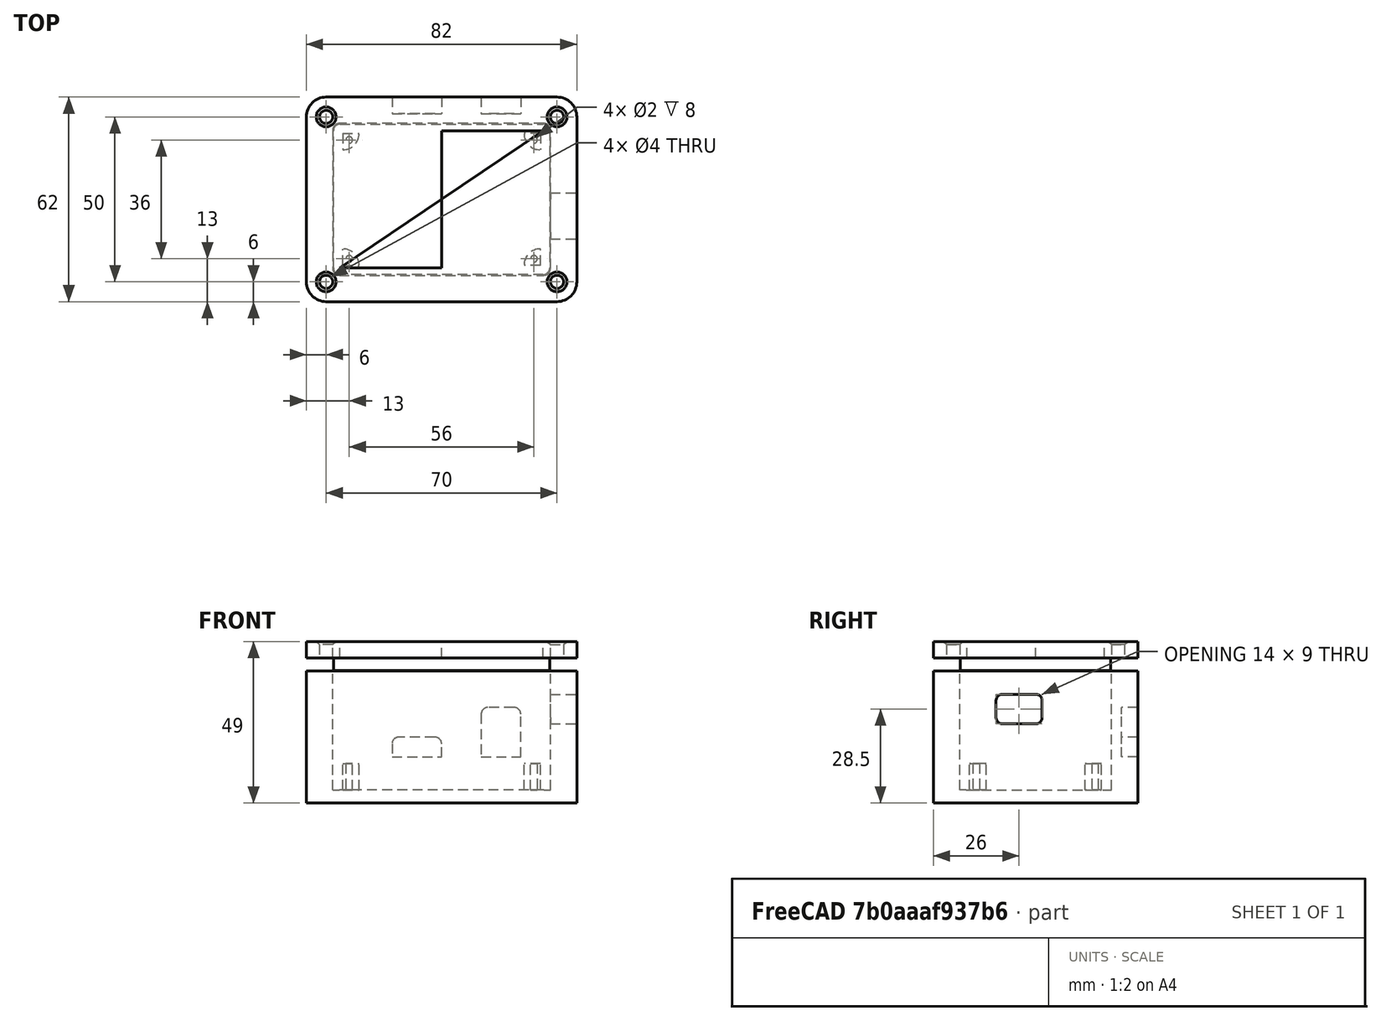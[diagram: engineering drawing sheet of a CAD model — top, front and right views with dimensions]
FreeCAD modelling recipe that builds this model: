
FCSTD DOCUMENT  (FreeCAD 0.20R29177 (Git))
Label: weatherstation
License: All rights reserved
LicenseURL: http://en.wikipedia.org/wiki/All_rights_reserved
objects: Sketcher::SketchObject×9, PartDesign::Pocket×5, PartDesign::Pad×4, PartDesign::Mirrored×4, PartDesign::MultiTransform×2, PartDesign::Body×2, Spreadsheet::Sheet×1, PartDesign::Chamfer×1
note: 37 computed .brp shape members not serialized (recipe doc carries the construction recipe); baked Part::Feature solids carry a one-line shape summary decoded from their .brp

FEATURE [Sketcher::SketchObject] Sketch  label="box"
  AttachmentOffset = pos=(0,0,-4) rot=(0,0,1;0rad)
  FullyConstrained = true
  MapMode = 5
  Placement = pos=(0,0,-4) rot=(0,0,1;0rad)
  Support = -> [XY_Plane]
  expr: .AttachmentOffset.Base.z = -Spreadsheet.box_wall_thickness
  expr: Constraints[16] = Spreadsheet.box_length
  expr: Constraints[17] = Spreadsheet.box_width
  expr: Constraints[18] = Spreadsheet.outside_radius
  sketch-geometry (8):
    g0: LineSegment StartX=-35 StartY=31 StartZ=0 EndX=35 EndY=31 EndZ=0
    g1: LineSegment StartX=41 StartY=25 StartZ=0 EndX=41 EndY=-25 EndZ=0
    g2: LineSegment StartX=35 StartY=-31 StartZ=0 EndX=-35 EndY=-31 EndZ=0
    g3: LineSegment StartX=-41 StartY=-25 StartZ=0 EndX=-41 EndY=25 EndZ=0
    g4: ArcOfCircle CenterX=-35 CenterY=25 CenterZ=0 NormalX=0 NormalY=0 NormalZ=1 AngleXU=0 Radius=6 StartAngle=1.5708 EndAngle=3.14159
    g5: ArcOfCircle CenterX=35 CenterY=25 CenterZ=0 NormalX=0 NormalY=0 NormalZ=1 AngleXU=0 Radius=6 StartAngle=-1.994e-12 EndAngle=1.5708
    g6: ArcOfCircle CenterX=35 CenterY=-25 CenterZ=0 NormalX=0 NormalY=0 NormalZ=1 AngleXU=0 Radius=6 StartAngle=4.71239 EndAngle=6.28319
    g7: ArcOfCircle CenterX=-35 CenterY=-25 CenterZ=0 NormalX=0 NormalY=0 NormalZ=1 AngleXU=0 Radius=6 StartAngle=3.14159 EndAngle=4.71239
  constraints (19):
    c: Horizontal(g0)
    c: Horizontal(g2)
    c: Vertical(g1)
    c: Vertical(g3)
    c: Tangent(g0,g4) = 1.5708
    c: Tangent(g3,g4) = 1.5708
    c: Tangent(g0,g5) = 1.5708
    c: Tangent(g1,g5) = 1.5708
    c: Tangent(g1,g6) = 1.5708
    c: Tangent(g2,g6) = 1.5708
    c: Tangent(g2,g7) = 1.5708
    c: Tangent(g3,g7) = 1.5708
    c: Equal(g4,g5)
    c: Equal(g5,g6)
    c: Equal(g6,g7)
    c: Symmetric(g4,g6,g-1)
    c: DistanceX(g0,g0) = 70
    c: DistanceY(g1,g1) = 50
    c: Radius(g4) = 6
FEATURE [PartDesign::Pad] Pad
  Direction = (0,0,1)
  Length = 40
  Length2 = 10
  Profile = -> Sketch
  ReferenceAxis = -> Sketch [N_Axis]
  Type = 0
  expr: Length = Spreadsheet.box_height
FEATURE [Spreadsheet::Sheet] Spreadsheet
  cells = A2=box_length; B2(box_length)=70; A3=box_width; B3(box_width)=50; A4=box_height; B4(box_height)=40; A5=outside_radius; B5(outside_radius)==B7 + 2; C5=Calculated; A6=inside_radius; B6(inside_radius)==B7 - 2; C6=Calculated; A7=box_wall_thickness; B7(box_wall_thickness)=4; A8=hole_diameter; B8(hole_diameter)=2; A9=lug_height; B9(lug_height)==B7 * 2; C9=Calculated; A10=lug_radius; B10(lug_radius)==B8 * 2.5; C10=Calculated; A11=hole_center_length; B11(hole_center_length)==B13 / 2 - B8; C11=Calculated; A12=hole_center_width; B12(hole_center_width)==B14 / 2 - B8; C12=Calculated; A13=box_inside_length; B13(box_inside_length)==B2 - 2 * B7; C13=Calculated; A14=box_inside_width; B14(box_inside_width)==B3 - 2 * B7; C14=Calculated; A16=clearance_sides; B16(clearance_sides)=0.2; A17=clearence_hole; B17==B8 + 2; A18=lid_height; B18==B4 / 8
FEATURE [Sketcher::SketchObject] Sketch001  label="pocket"
  FullyConstrained = true
  MapMode = 5
  Support = -> [XY_Plane]
  expr: Constraints[16] = Spreadsheet.box_inside_length
  expr: Constraints[17] = Spreadsheet.box_inside_width
  expr: Constraints[18] = Spreadsheet.inside_radius
  sketch-geometry (8):
    g0: LineSegment StartX=-31 StartY=23 StartZ=0 EndX=31 EndY=23 EndZ=0
    g1: LineSegment StartX=33 StartY=21 StartZ=0 EndX=33 EndY=-21 EndZ=0
    g2: LineSegment StartX=31 StartY=-23 StartZ=0 EndX=-31 EndY=-23 EndZ=0
    g3: LineSegment StartX=-33 StartY=-21 StartZ=0 EndX=-33 EndY=21 EndZ=0
    g4: ArcOfCircle CenterX=-31 CenterY=21 CenterZ=0 NormalX=0 NormalY=0 NormalZ=1 AngleXU=0 Radius=2 StartAngle=1.5708 EndAngle=3.14159
    g5: ArcOfCircle CenterX=31 CenterY=21 CenterZ=0 NormalX=0 NormalY=0 NormalZ=1 AngleXU=0 Radius=2 StartAngle=-9e-16 EndAngle=1.5708
    g6: ArcOfCircle CenterX=31 CenterY=-21 CenterZ=0 NormalX=0 NormalY=0 NormalZ=1 AngleXU=0 Radius=2 StartAngle=4.71239 EndAngle=6.28319
    g7: ArcOfCircle CenterX=-31 CenterY=-21 CenterZ=0 NormalX=0 NormalY=0 NormalZ=1 AngleXU=0 Radius=2 StartAngle=3.14159 EndAngle=4.71239
  constraints (19):
    c: Horizontal(g0)
    c: Horizontal(g2)
    c: Vertical(g1)
    c: Vertical(g3)
    c: Tangent(g0,g4) = 1.5708
    c: Tangent(g3,g4) = 1.5708
    c: Tangent(g0,g5) = 1.5708
    c: Tangent(g1,g5) = 1.5708
    c: Tangent(g1,g6) = 1.5708
    c: Tangent(g2,g6) = 1.5708
    c: Tangent(g2,g7) = 1.5708
    c: Tangent(g3,g7) = 1.5708
    c: Symmetric(g4,g6,g-1)
    c: Equal(g4,g5)
    c: Equal(g5,g6)
    c: Equal(g6,g7)
    c: DistanceX(g0,g0) = 62
    c: DistanceY(g1,g1) = 42
    c: Radius(g4) = 2
FEATURE [PartDesign::Pocket] Pocket
  BaseFeature = -> Pad
  Direction = (0,0,-1)
  Length = 5
  Length2 = 5
  Profile = -> Sketch001
  ReferenceAxis = -> Sketch001 [N_Axis]
  Reversed = true
  Type = 1
FEATURE [Sketcher::SketchObject] Sketch002  label="lug"
  FullyConstrained = true
  MapMode = 5
  Support = -> [XY_Plane]
  expr: Constraints[10] = Spreadsheet.hole_center_length - 1
  expr: Constraints[11] = Spreadsheet.hole_center_width - 1
  expr: Constraints[6] = Spreadsheet.hole_diameter
  expr: Constraints[7] = Spreadsheet.lug_radius
  expr: Constraints[8] = Spreadsheet.hole_diameter
  expr: Constraints[9] = Spreadsheet.hole_diameter
  sketch-geometry (4):
    g0: LineSegment StartX=-30 StartY=20 StartZ=0 EndX=-25 EndY=20 EndZ=0
    g1: LineSegment StartX=-30 StartY=20 StartZ=0 EndX=-30 EndY=15 EndZ=0
    g2: ArcOfCircle CenterX=-30 CenterY=20 CenterZ=0 NormalX=0 NormalY=0 NormalZ=1 AngleXU=0 Radius=5 StartAngle=4.71239 EndAngle=6.28319
    g3: Circle CenterX=-28 CenterY=18 CenterZ=0 NormalX=0 NormalY=0 NormalZ=1 AngleXU=0 Radius=1
  constraints (12):
    c: Horizontal(g0)
    c: Coincident(g1,g0)
    c: Vertical(g1)
    c: Coincident(g2,g0)
    c: Coincident(g2,g0)
    c: Coincident(g2,g1)
    c: Diameter(g3) = 2
    c: Radius(g2) = 5
    c: DistanceY(g3,g0) = 2
    c: DistanceX(g0,g3) = 2
    c: DistanceX(g3,g-1) = 28
    c: DistanceY(g-1,g3) = 18
FEATURE [PartDesign::Pad] Pad001
  BaseFeature = -> Pocket
  Direction = (0,0,1)
  Length = 8
  Length2 = 10
  Profile = -> Sketch002
  ReferenceAxis = -> Sketch002 [N_Axis]
  Type = 0
  expr: Length = Spreadsheet.lug_height
FEATURE [PartDesign::Mirrored] Mirrored
  MirrorPlane = -> Sketch002 [V_Axis]
FEATURE [PartDesign::Mirrored] Mirrored001
  MirrorPlane = -> Sketch002 [H_Axis]
FEATURE [PartDesign::MultiTransform] MultiTransform
  BaseFeature = -> Pad001
  Originals = -> [Pad001]
  Transformations = -> [Mirrored,Mirrored001]
FEATURE [Sketcher::SketchObject] Sketch003  label="usbInlet"
  FullyConstrained = true
  MapMode = 5
  Placement = pos=(0,0,0) rot=(0.57735,0.57735,0.57735;2.0944rad)
  Support = -> [YZ_Plane]
  expr: Constraints[18] = 0
  expr: Constraints[19] = Spreadsheet.lug_height + 12
  sketch-geometry (8):
    g0: LineSegment StartX=-2e-16 StartY=20 StartZ=0 EndX=-10 EndY=20 EndZ=0
    g1: LineSegment StartX=-12 StartY=22 StartZ=0 EndX=-12 EndY=27 EndZ=0
    g2: LineSegment StartX=-10 StartY=29 StartZ=0 EndX=0 EndY=29 EndZ=0
    g3: LineSegment StartX=2 StartY=27 StartZ=0 EndX=2 EndY=22 EndZ=0
    g4: ArcOfCircle CenterX=-10 CenterY=27 CenterZ=0 NormalX=0 NormalY=0 NormalZ=1 AngleXU=0 Radius=2 StartAngle=1.5708 EndAngle=3.14159
    g5: ArcOfCircle CenterX=2e-16 CenterY=27 CenterZ=0 NormalX=0 NormalY=0 NormalZ=1 AngleXU=0 Radius=2 StartAngle=4e-16 EndAngle=1.5708
    g6: ArcOfCircle CenterX=2e-16 CenterY=22 CenterZ=0 NormalX=0 NormalY=0 NormalZ=1 AngleXU=0 Radius=2 StartAngle=4.71239 EndAngle=6.28319
    g7: ArcOfCircle CenterX=-10 CenterY=22 CenterZ=0 NormalX=0 NormalY=0 NormalZ=1 AngleXU=0 Radius=2 StartAngle=3.14159 EndAngle=4.71239
  constraints (20):
    c: Horizontal(g0)
    c: Horizontal(g2)
    c: Vertical(g1)
    c: Vertical(g3)
    c: Tangent(g1,g4) = 1.5708
    c: Tangent(g2,g4) = 1.5708
    c: Tangent(g2,g5) = 1.5708
    c: Tangent(g3,g5) = 1.5708
    c: Tangent(g0,g6) = 1.5708
    c: Tangent(g3,g6) = 1.5708
    c: Tangent(g0,g7) = 1.5708
    c: Tangent(g1,g7) = 1.5708
    c: Equal(g4,g5)
    c: Equal(g5,g6)
    c: Equal(g6,g7)
    c: Radius(g4) = 2
    c: DistanceX(g2,g2) = 10
    c: DistanceY(g3,g3) = 5
    c: DistanceX(g-1,g0) = 0
    c: DistanceY(g-1,g0) = 20
FEATURE [PartDesign::Pocket] Pocket001
  BaseFeature = -> MultiTransform
  Direction = (-1,2e-16,-3e-16)
  Length = 5
  Length2 = 5
  Profile = -> Sketch003
  ReferenceAxis = -> Sketch003 [N_Axis]
  Reversed = true
  Type = 1
FEATURE [Sketcher::SketchObject] Sketch004  label="SensorAndConnectorHoles"
  FullyConstrained = true
  MapMode = 5
  Placement = pos=(0,31,0) rot=(0,0.707107,0.707107;3.14159rad)
  Support = -> [Pocket001]
  expr: Constraints[16] = Spreadsheet.lug_height + 2
  expr: Constraints[17] = Spreadsheet.lug_height + 2
  sketch-geometry (12):
    g0: LineSegment StartX=-22 StartY=25 StartZ=0 EndX=-14 EndY=25 EndZ=0
    g1: LineSegment StartX=-12 StartY=23 StartZ=0 EndX=-12 EndY=10 EndZ=0
    g2: LineSegment StartX=-12 StartY=10 StartZ=0 EndX=-24 EndY=10 EndZ=0
    g3: LineSegment StartX=-24 StartY=10 StartZ=0 EndX=-24 EndY=23 EndZ=0
    g4: LineSegment StartX=2 StartY=16 StartZ=0 EndX=13 EndY=16 EndZ=0
    g5: LineSegment StartX=15 StartY=14 StartZ=0 EndX=15 EndY=10 EndZ=0
    g6: LineSegment StartX=15 StartY=10 StartZ=0 EndX=1.8e-15 EndY=10 EndZ=0
    g7: LineSegment StartX=1.8e-15 StartY=10 StartZ=0 EndX=1.8e-15 EndY=14 EndZ=0
    g8: ArcOfCircle CenterX=-22 CenterY=23 CenterZ=0 NormalX=0 NormalY=0 NormalZ=1 AngleXU=0 Radius=2 StartAngle=1.5708 EndAngle=3.14159
    g9: ArcOfCircle CenterX=-14 CenterY=23 CenterZ=0 NormalX=0 NormalY=0 NormalZ=1 AngleXU=0 Radius=2 StartAngle=2e-16 EndAngle=1.5708
    g10: ArcOfCircle CenterX=2 CenterY=14 CenterZ=0 NormalX=0 NormalY=0 NormalZ=1 AngleXU=0 Radius=2 StartAngle=1.5708 EndAngle=3.14159
    g11: ArcOfCircle CenterX=13 CenterY=14 CenterZ=0 NormalX=0 NormalY=0 NormalZ=1 AngleXU=0 Radius=2 StartAngle=0 EndAngle=1.5708
  constraints (32):
    c: Coincident(g1,g2)
    c: Coincident(g2,g3)
    c: Horizontal(g0)
    c: Horizontal(g2)
    c: Vertical(g1)
    c: Vertical(g3)
    c: DistanceX(g1,g-1) = 12
    c: DistanceX(g2,g1) = 12
    c: Coincident(g5,g6)
    c: Coincident(g6,g7)
    c: Horizontal(g4)
    c: Horizontal(g6)
    c: Vertical(g5)
    c: Vertical(g7)
    c: DistanceX(g-1,g6) = 0
    c: DistanceX(g6,g5) = 15
    c: DistanceY(g-1,g1) = 10
    c: DistanceY(g-1,g6) = 10
    c: Tangent(g0,g8) = 1.5708
    c: Tangent(g3,g8) = 1.5708
    c: Tangent(g0,g9) = 1.5708
    c: Tangent(g1,g9) = 1.5708
    c: Tangent(g4,g10) = 1.5708
    c: Tangent(g7,g10) = 1.5708
    c: Tangent(g4,g11) = 1.5708
    c: Tangent(g5,g11) = 1.5708
    c: Equal(g9,g8)
    c: Equal(g10,g11)
    c: Radius(g8) = 2
    c: Radius(g11) = 2
    c: DistanceY(g1,g0) = 15
    c: DistanceY(g5,g4) = 6
FEATURE [PartDesign::Pocket] Pocket002
  BaseFeature = -> Pocket001
  Direction = (0,-1,2e-16)
  Length = 5
  Length2 = 5
  Profile = -> Sketch004
  ReferenceAxis = -> Sketch004 [N_Axis]
  Type = 0
FEATURE [PartDesign::Body] Body  label="Box"
  Group = -> [Sketch,Pad,Sketch001,Pocket,Sketch002,Pad001,MultiTransform,Mirrored,Mirrored001,Sketch003,Pocket001,Sketch004,Pocket002]
  Origin = -> Origin
  Tip = -> Pocket002
FEATURE [Sketcher::SketchObject] Sketch005
  AttachmentOffset = pos=(0,0,40) rot=(0,0,1;0rad)
  FullyConstrained = true
  MapMode = 5
  Placement = pos=(0,0,40) rot=(0,0,1;0rad)
  Support = -> [XY_Plane001]
  expr: .AttachmentOffset.Base.z = Spreadsheet.box_height
  expr: Constraints[12] = Spreadsheet.box_length
  expr: Constraints[13] = Spreadsheet.box_width
  expr: Constraints[17] = Spreadsheet.outside_radius
  sketch-geometry (8):
    g0: LineSegment StartX=-35 StartY=31 StartZ=0 EndX=35 EndY=31 EndZ=0
    g1: LineSegment StartX=41 StartY=25 StartZ=0 EndX=41 EndY=-25 EndZ=0
    g2: LineSegment StartX=35 StartY=-31 StartZ=0 EndX=-35 EndY=-31 EndZ=0
    g3: LineSegment StartX=-41 StartY=-25 StartZ=0 EndX=-41 EndY=25 EndZ=0
    g4: ArcOfCircle CenterX=-35 CenterY=25 CenterZ=0 NormalX=0 NormalY=0 NormalZ=1 AngleXU=0 Radius=6 StartAngle=1.5708 EndAngle=3.14159
    g5: ArcOfCircle CenterX=35 CenterY=25 CenterZ=0 NormalX=0 NormalY=0 NormalZ=1 AngleXU=0 Radius=6 StartAngle=0 EndAngle=1.5708
    g6: ArcOfCircle CenterX=35 CenterY=-25 CenterZ=0 NormalX=0 NormalY=0 NormalZ=1 AngleXU=0 Radius=6 StartAngle=4.71239 EndAngle=6.28319
    g7: ArcOfCircle CenterX=-35 CenterY=-25 CenterZ=0 NormalX=0 NormalY=0 NormalZ=1 AngleXU=0 Radius=6 StartAngle=3.14159 EndAngle=4.71239
  constraints (19):
    c: Horizontal(g0)
    c: Horizontal(g2)
    c: Vertical(g1)
    c: Vertical(g3)
    c: Tangent(g0,g4) = 1.5708
    c: Tangent(g3,g4) = 1.5708
    c: Tangent(g0,g5) = 1.5708
    c: Tangent(g1,g5) = 1.5708
    c: Tangent(g1,g6) = 1.5708
    c: Tangent(g2,g6) = 1.5708
    c: Tangent(g2,g7) = 1.5708
    c: Tangent(g3,g7) = 1.5708
    c: DistanceX(g0,g0) = 70
    c: DistanceY(g1,g1) = 50
    c: Equal(g5,g6)
    c: Equal(g6,g7)
    c: Equal(g7,g4)
    c: Radius(g4) = 6
    c: Symmetric(g0,g2,g-1)
FEATURE [PartDesign::Pad] Pad002
  Direction = (0,0,1)
  Length = 5
  Length2 = 10
  Profile = -> Sketch005
  ReferenceAxis = -> Sketch005 [N_Axis]
  Type = 0
  expr: Length = 5
FEATURE [Sketcher::SketchObject] Sketch006
  AttachmentOffset = pos=(0,0,40) rot=(0,0,1;0rad)
  FullyConstrained = true
  MapMode = 5
  Placement = pos=(0,0,40) rot=(0,0,1;0rad)
  Support = -> [XY_Plane001]
  expr: .AttachmentOffset.Base.z = Spreadsheet.box_height
  expr: Constraints[16] = Spreadsheet.inside_radius
  expr: Constraints[17] = Spreadsheet.box_inside_length - Spreadsheet.clearance_sides * 2
  expr: Constraints[18] = Spreadsheet.box_inside_width - Spreadsheet.clearance_sides * 2
  sketch-geometry (8):
    g0: LineSegment StartX=-30.8 StartY=22.8 StartZ=0 EndX=30.8 EndY=22.8 EndZ=0
    g1: LineSegment StartX=32.8 StartY=20.8 StartZ=0 EndX=32.8 EndY=-20.8 EndZ=0
    g2: LineSegment StartX=30.8 StartY=-22.8 StartZ=0 EndX=-30.8 EndY=-22.8 EndZ=0
    g3: LineSegment StartX=-32.8 StartY=-20.8 StartZ=0 EndX=-32.8 EndY=20.8 EndZ=0
    g4: ArcOfCircle CenterX=-30.8 CenterY=20.8 CenterZ=0 NormalX=0 NormalY=0 NormalZ=1 AngleXU=0 Radius=2 StartAngle=1.5708 EndAngle=3.14159
    g5: ArcOfCircle CenterX=30.8 CenterY=20.8 CenterZ=0 NormalX=0 NormalY=0 NormalZ=1 AngleXU=0 Radius=2 StartAngle=-9e-16 EndAngle=1.5708
    g6: ArcOfCircle CenterX=30.8 CenterY=-20.8 CenterZ=0 NormalX=0 NormalY=0 NormalZ=1 AngleXU=0 Radius=2 StartAngle=4.71239 EndAngle=6.28319
    g7: ArcOfCircle CenterX=-30.8 CenterY=-20.8 CenterZ=0 NormalX=0 NormalY=0 NormalZ=1 AngleXU=0 Radius=2 StartAngle=3.14159 EndAngle=4.71239
  constraints (19):
    c: Horizontal(g0)
    c: Horizontal(g2)
    c: Vertical(g1)
    c: Vertical(g3)
    c: Tangent(g0,g4) = 1.5708
    c: Tangent(g3,g4) = 1.5708
    c: Tangent(g0,g5) = 1.5708
    c: Tangent(g1,g5) = 1.5708
    c: Tangent(g1,g6) = 1.5708
    c: Tangent(g2,g6) = 1.5708
    c: Tangent(g2,g7) = 1.5708
    c: Tangent(g3,g7) = 1.5708
    c: Symmetric(g6,g4,g-1)
    c: Equal(g4,g5)
    c: Equal(g5,g6)
    c: Equal(g6,g7)
    c: Radius(g4) = 2
    c: DistanceX(g0,g0) = 61.6
    c: DistanceY(g1,g1) = 41.6
FEATURE [PartDesign::Pad] Pad003
  BaseFeature = -> Pad002
  Direction = (0,0,1)
  Length = 3.8
  Length2 = 10
  Profile = -> Sketch006
  ReferenceAxis = -> Sketch006 [N_Axis]
  Reversed = true
  Type = 0
  expr: Length = Spreadsheet.box_wall_thickness - Spreadsheet.clearance_sides
FEATURE [Sketcher::SketchObject] Sketch008
  FullyConstrained = true
  MapMode = 5
  Support = -> [XY_Plane001]
  expr: Constraints[0] = Spreadsheet.hole_diameter + 2
  expr: Constraints[1] = Spreadsheet.box_length / 2
  expr: Constraints[2] = Spreadsheet.box_width / 2
  sketch-geometry (1):
    g0: Circle CenterX=-35 CenterY=25 CenterZ=0 NormalX=0 NormalY=0 NormalZ=1 AngleXU=0 Radius=2
  constraints (3):
    c: Diameter(g0) = 4
    c: DistanceX(g0,g-1) = 35
    c: DistanceY(g-1,g0) = 25
FEATURE [PartDesign::Pocket] Pocket003
  BaseFeature = -> Pad003
  Direction = (0,0,-1)
  Length = 5
  Length2 = 5
  Profile = -> Sketch008
  ReferenceAxis = -> Sketch008 [N_Axis]
  Reversed = true
  Type = 1
FEATURE [PartDesign::Mirrored] Mirrored002
  MirrorPlane = -> XZ_Plane001
FEATURE [PartDesign::Mirrored] Mirrored003
  MirrorPlane = -> YZ_Plane001
FEATURE [PartDesign::MultiTransform] MultiTransform001
  BaseFeature = -> Pocket003
  Originals = -> [Pocket003]
  Transformations = -> [Mirrored002,Mirrored003]
FEATURE [PartDesign::Chamfer] Chamfer
  Angle = 45
  Base = -> MultiTransform001 [Edge33,Edge35,Edge36,Edge34]
  BaseFeature = -> MultiTransform001
  ChamferType = 0
  FlipDirection = false
  Size = 1
  Size2 = 1
  SupportTransform = false
  UseAllEdges = false
FEATURE [Sketcher::SketchObject] Sketch010
  AttachmentOffset = pos=(0,0,40) rot=(0,0,1;0rad)
  FullyConstrained = true
  MapMode = 5
  Placement = pos=(0,0,40) rot=(0,0,1;0rad)
  Support = -> [XY_Plane001]
  expr: .AttachmentOffset.Base.z = Spreadsheet.box_height
  expr: Constraints[12] = Spreadsheet.box_inside_length / 2 - Spreadsheet.clearance_sides
  expr: Constraints[15] = Spreadsheet.box_inside_width / 2 - Spreadsheet.clearance_sides
  sketch-geometry (6):
    g0: LineSegment StartX=0 StartY=0 StartZ=0 EndX=30.8 EndY=20.8 EndZ=0
    g1: LineSegment StartX=0 StartY=0 StartZ=0 EndX=-30.8 EndY=-20.8 EndZ=0
    g2: LineSegment StartX=-30.8 StartY=-20.8 StartZ=0 EndX=0 EndY=-20.8 EndZ=0
    g3: LineSegment StartX=0 StartY=0 StartZ=0 EndX=0 EndY=-20.8 EndZ=0
    g4: LineSegment StartX=0 StartY=0 StartZ=0 EndX=0 EndY=20.8 EndZ=0
    g5: LineSegment StartX=30.8 StartY=20.8 StartZ=0 EndX=0 EndY=20.8 EndZ=0
  constraints (16):
    c: Coincident(g0,g-1)
    c: Coincident(g1,g0)
    c: Coincident(g2,g1)
    c: PointOnObject(g2,g-2)
    c: Horizontal(g2)
    c: Coincident(g3,g0)
    c: Coincident(g3,g2)
    c: Coincident(g4,g0)
    c: PointOnObject(g4,g-2)
    c: Coincident(g5,g0)
    c: Coincident(g5,g4)
    c: Horizontal(g5)
    c: DistanceX(g2,g2) = 30.8
    c: Equal(g2,g5)
    c: Equal(g3,g4)
    c: DistanceY(g4,g4) = 20.8
FEATURE [PartDesign::Pocket] Pocket004
  BaseFeature = -> Chamfer
  Direction = (0,0,-1)
  Length = 5
  Length2 = 5
  Profile = -> Sketch010
  ReferenceAxis = -> Sketch010 [N_Axis]
  Reversed = true
  Type = 1
FEATURE [PartDesign::Body] Body001  label="Lid"
  Group = -> [Sketch005,Pad002,Sketch006,Pad003,Sketch008,Pocket003,MultiTransform001,Mirrored002,Mirrored003,Chamfer,Sketch010,Pocket004]
  Origin = -> Origin001
  Tip = -> Pocket004
